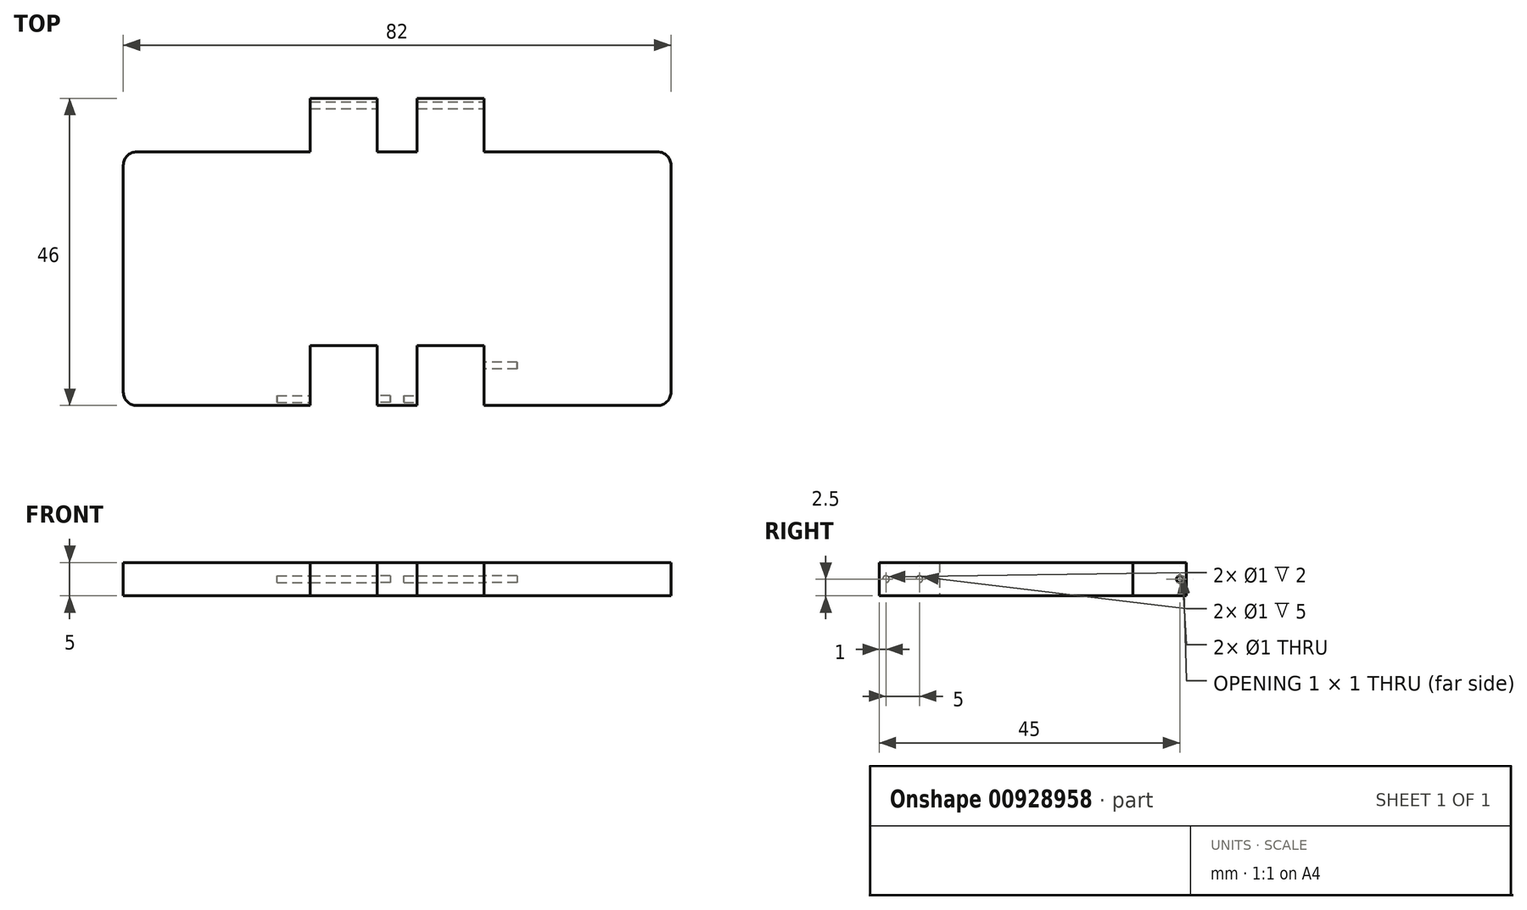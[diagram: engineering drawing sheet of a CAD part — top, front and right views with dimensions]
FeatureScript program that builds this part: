
annotation { "Feature Type Name" : "Feature", "Feature Type Description" : "" }
export const myFeature = defineFeature(function(context is Context, id is Id, definition is map)
    precondition{}
    {
        {
            var Q0;
            Q0=qCreatedBy(makeId("Top.planeOp"),FACE);
            var sketch = newSketch(context, id + "F0", { "sketchPlane" : qUnion([Q0])});
            skLineSegment(sketch, "E0", {"start": v(0, 37.61) * mm, "end": v(0, -36.93) * mm, "construction": true});
            skLineSegment(sketch, "E1", {"start": v(-42.57, 0) * mm, "end": v(44.57, 0) * mm, "construction": true});
            skLineSegment(sketch, "E2", {"start": v(-41, 17) * mm, "end": v(-41, -17) * mm});
            skLineSegment(sketch, "E3", {"start": v(-39, -19) * mm, "end": v(-13, -19) * mm});
            skLineSegment(sketch, "E4", {"start": v(-13, -19) * mm, "end": v(-13, -10) * mm});
            skLineSegment(sketch, "E5", {"start": v(13, -10) * mm, "end": v(13, -19) * mm});
            skLineSegment(sketch, "E6", {"start": v(13, -19) * mm, "end": v(39, -19) * mm});
            skLineSegment(sketch, "E7", {"start": v(41, -17) * mm, "end": v(41, 17) * mm});
            skLineSegment(sketch, "E8", {"start": v(-13, -10) * mm, "end": v(-3, -10) * mm});
            skLineSegment(sketch, "E9", {"start": v(-3, -10) * mm, "end": v(-3, -19) * mm});
            skLineSegment(sketch, "E10", {"start": v(-3, -19) * mm, "end": v(3, -19) * mm});
            skLineSegment(sketch, "E11", {"start": v(3, -19) * mm, "end": v(3, -10) * mm});
            skLineSegment(sketch, "E12", {"start": v(3, -10) * mm, "end": v(13, -10) * mm});
            skPoint(sketch, "E13.visualSharp", {"position": v(-41, 19) * mm});
            skArc(sketch, "E13.filletArc", {"start": v(-39, 19) * mm, "mid": v(-40.41, 18.41) * mm, "end": v(-41, 17) * mm});
            skPoint(sketch, "E14.visualSharp", {"position": v(-41, -19) * mm});
            skArc(sketch, "E14.filletArc", {"start": v(-41, -17) * mm, "mid": v(-40.41, -18.41) * mm, "end": v(-39, -19) * mm});
            skPoint(sketch, "E15.visualSharp", {"position": v(41, 19) * mm});
            skArc(sketch, "E15.filletArc", {"start": v(41, 17) * mm, "mid": v(40.41, 18.41) * mm, "end": v(39, 19) * mm});
            skPoint(sketch, "E16.visualSharp", {"position": v(41, -19) * mm});
            skArc(sketch, "E16.filletArc", {"start": v(39, -19) * mm, "mid": v(40.41, -18.41) * mm, "end": v(41, -17) * mm});
            skLineSegment(sketch, "E17", {"start": v(-39, 19) * mm, "end": v(-13, 19) * mm});
            skLineSegment(sketch, "E18", {"start": v(-13, 19) * mm, "end": v(-13, 27) * mm});
            skLineSegment(sketch, "E19", {"start": v(-13, 27) * mm, "end": v(-3, 27) * mm});
            skLineSegment(sketch, "E20", {"start": v(-3, 27) * mm, "end": v(-3, 19) * mm});
            skLineSegment(sketch, "E21", {"start": v(-3, 19) * mm, "end": v(3, 19) * mm});
            skLineSegment(sketch, "E22", {"start": v(3, 19) * mm, "end": v(3, 27) * mm});
            skLineSegment(sketch, "E23", {"start": v(3, 27) * mm, "end": v(13, 27) * mm});
            skLineSegment(sketch, "E24", {"start": v(13, 27) * mm, "end": v(13, 19) * mm});
            skLineSegment(sketch, "E25", {"start": v(13, 19) * mm, "end": v(39, 19) * mm});
            skSolve(sketch);
        }
        {
            var Q0;
            Q0 = qSketchRegion(id + "F0", true);
            extrude(context, id + "F1", {"entities" : qUnion([Q0]), "depth" : 5 * mm, "offsetDistance" : 25.4 * mm});
        }
        {
            var Q0;
            Q0=makeQuery(id+"F1.opExtrude","SWEPT_FACE",FACE,{"disambiguationData":[OSD([sQuery(id+"F0.wireOp",EDGE,"E11")])]});
            var sketch = newSketch(context, id + "F2", { "sketchPlane" : qUnion([Q0])});
            skCircle(sketch, "E26", {"center": v(-18, 2.5) * mm, "radius": 0.5 * mm});
            skPoint(sketch, "E26.centerSnap0", {"position": v(-19, 2.5) * mm});
            skSolve(sketch);
        }
        {
            var Q0;
            Q0 = qSketchRegion(id + "F2", true);
            extrude(context, id + "F3", {"entities" : qUnion([Q0]), "operationType" : NewBodyOperationType.REMOVE, "oppositeDirection" : true, "depth" : 2 * mm, "offsetDistance" : 25.4 * mm});
        }
        {
            var Q0;
            Q0=makeQuery(id+"F1.opExtrude","SWEPT_FACE",FACE,{"disambiguationData":[OSD([sQuery(id+"F0.wireOp",EDGE,"E5")])]});
            var sketch = newSketch(context, id + "F4", { "sketchPlane" : qUnion([Q0])});
            skCircle(sketch, "E27", {"center": v(13, 2.5) * mm, "radius": 0.5 * mm});
            skPoint(sketch, "E27.centerSnap0", {"position": v(19, 2.5) * mm});
            skSolve(sketch);
        }
        {
            var Q0;
            Q0 = qSketchRegion(id + "F4", true);
            extrude(context, id + "F5", {"entities" : qUnion([Q0]), "operationType" : NewBodyOperationType.REMOVE, "oppositeDirection" : true, "depth" : 5 * mm, "offsetDistance" : 25.4 * mm});
        }
        {
            var Q0;
            Q0=makeQuery(id+"F1.opExtrude","SWEPT_FACE",FACE,{"disambiguationData":[OSD([sQuery(id+"F0.wireOp",EDGE,"E9")])]});
            var sketch = newSketch(context, id + "F6", { "sketchPlane" : qUnion([Q0])});
            skCircle(sketch, "E28", {"center": v(18, 2.5) * mm, "radius": 0.5 * mm});
            skPoint(sketch, "E28.centerSnap0", {"position": v(19, 2.5) * mm});
            skSolve(sketch);
        }
        {
            var Q0;
            Q0 = qSketchRegion(id + "F6", true);
            extrude(context, id + "F7", {"entities" : qUnion([Q0]), "operationType" : NewBodyOperationType.REMOVE, "oppositeDirection" : true, "depth" : 2 * mm, "offsetDistance" : 25.4 * mm});
        }
        {
            var Q0;
            Q0=makeQuery(id+"F1.opExtrude","SWEPT_FACE",FACE,{"disambiguationData":[OSD([sQuery(id+"F0.wireOp",EDGE,"E4")])]});
            var sketch = newSketch(context, id + "F8", { "sketchPlane" : qUnion([Q0])});
            skCircle(sketch, "E29", {"center": v(-18, 2.5) * mm, "radius": 0.5 * mm});
            skPoint(sketch, "E29.centerSnap0", {"position": v(-19, 2.5) * mm});
            skSolve(sketch);
        }
        {
            var Q0;
            Q0 = qSketchRegion(id + "F8", true);
            extrude(context, id + "F9", {"entities" : qUnion([Q0]), "operationType" : NewBodyOperationType.REMOVE, "oppositeDirection" : true, "depth" : 5 * mm, "offsetDistance" : 25.4 * mm});
        }
        {
            var Q0;
            Q0=qCreatedBy(makeId("Right.planeOp"),FACE);
            var sketch = newSketch(context, id + "F10", { "sketchPlane" : qUnion([Q0])});
            skCircle(sketch, "E30", {"center": v(26, 2.5) * mm, "radius": 0.5 * mm});
            skSolve(sketch);
        }
        {
            var Q0;
            Q0 = qSketchRegion(id + "F10", true);
            extrude(context, id + "F11", {"entities" : qUnion([Q0]), "operationType" : NewBodyOperationType.REMOVE, "endBound" : BoundingType.SYMMETRIC, "oppositeDirection" : true, "depth" : 28.96 * mm, "offsetDistance" : 25.4 * mm});
        }
    });
